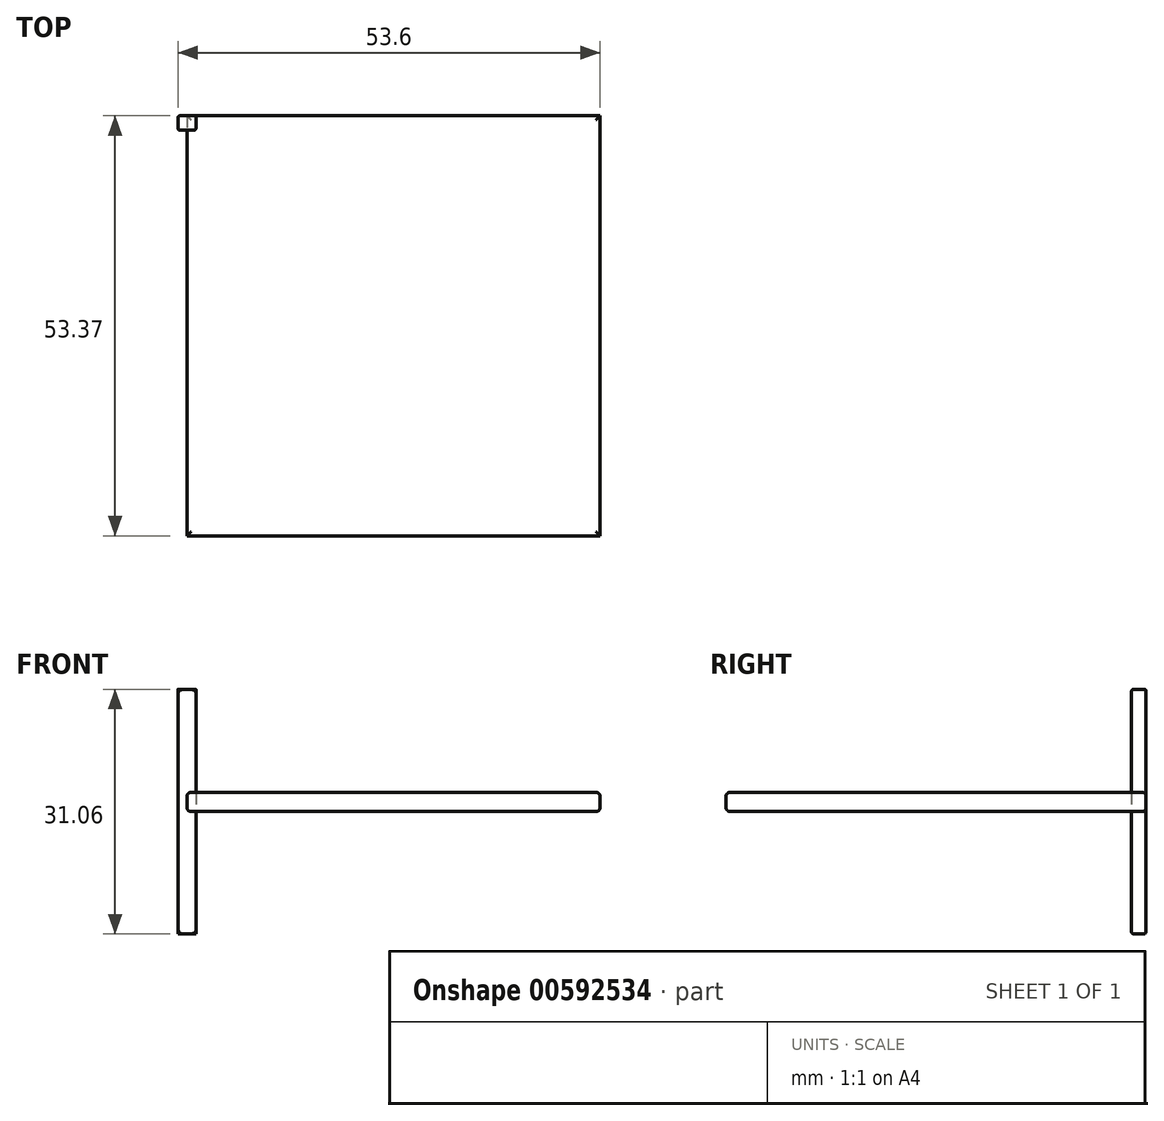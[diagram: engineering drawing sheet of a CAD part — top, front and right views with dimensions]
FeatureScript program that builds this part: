
annotation { "Feature Type Name" : "Feature", "Feature Type Description" : "" }
export const myFeature = defineFeature(function(context is Context, id is Id, definition is map)
    precondition{}
    {
        {
            var Q0;
            Q0=qCreatedBy(makeId("Front.planeOp"),FACE);
            var sketch = newSketch(context, id + "F0", { "sketchPlane" : qUnion([Q0])});
            skLineSegment(sketch, "E0.bottom", {"start": v(-76.14, -76.26) * mm, "end": v(-73.88, -76.26) * mm});
            skLineSegment(sketch, "E0.top", {"start": v(-76.14, -107.32) * mm, "end": v(-73.88, -107.32) * mm});
            skLineSegment(sketch, "E0.left", {"start": v(-76.14, -76.26) * mm, "end": v(-76.14, -107.32) * mm});
            skLineSegment(sketch, "E0.right", {"start": v(-73.88, -76.26) * mm, "end": v(-73.88, -107.32) * mm});
            skLineSegment(sketch, "E1.bottom", {"start": v(-1.13, 15.53) * mm, "end": v(1.13, 15.53) * mm});
            skLineSegment(sketch, "E1.top", {"start": v(-1.13, -15.53) * mm, "end": v(1.13, -15.53) * mm});
            skLineSegment(sketch, "E1.left", {"start": v(-1.13, 15.53) * mm, "end": v(-1.13, -15.53) * mm});
            skLineSegment(sketch, "E1.right", {"start": v(1.13, 15.53) * mm, "end": v(1.13, -15.53) * mm});
            skSolve(sketch);
        }
        {
            var Q0;
            Q0 = qSketchRegion(id + "F0", true);
            extrude(context, id + "F1", {"entities" : qUnion([Q0]), "depth" : 1.86 * mm, "offsetDistance" : 25.4 * mm});
        }
        {
            var Q0;
            Q0=qCreatedBy(makeId("Top.planeOp"),FACE);
            var sketch = newSketch(context, id + "F2", { "sketchPlane" : qUnion([Q0])});
            skLineSegment(sketch, "E2.bottom", {"start": v(0, 0) * mm, "end": v(52.47, 0) * mm});
            skLineSegment(sketch, "E2.top", {"start": v(0, -53.37) * mm, "end": v(52.47, -53.37) * mm});
            skLineSegment(sketch, "E2.left", {"start": v(0, 0) * mm, "end": v(0, -53.37) * mm});
            skLineSegment(sketch, "E2.right", {"start": v(52.47, 0) * mm, "end": v(52.47, -53.37) * mm});
            skSolve(sketch);
        }
        {
            var Q0;
            Q0 = qSketchRegion(id + "F2", true);
            extrude(context, id + "F3", {"entities" : qUnion([Q0]), "depth" : 2.44 * mm, "offsetDistance" : 25.4 * mm});
        }
        {
            var Q0;
            Q0=makeQuery(id+"F1.opExtrude","SWEPT_BODY",BODY,{"disambiguationData":[OSD([sQuery(id+"F0.wireOp",EDGE,"E0.bottom"),sQuery(id+"F0.wireOp",EDGE,"E0.top"),sQuery(id+"F0.wireOp",EDGE,"E0.left"),sQuery(id+"F0.wireOp",EDGE,"E0.right")])]});
            deleteBodies(context, id + "F4", {"entities" : qUnion([Q0])});
        }
        {
            var Q0;
            Q0=makeQuery(id+"F3.opExtrude","CAP_FACE",FACE,{"disambiguationData":[OSD([sQuery(id+"F2.wireOp",EDGE,"E2.bottom"),sQuery(id+"F2.wireOp",EDGE,"E2.top"),sQuery(id+"F2.wireOp",EDGE,"E2.left"),sQuery(id+"F2.wireOp",EDGE,"E2.right")])],"isStart":false});
            var Q1;
            Q1=makeQuery(id+"F3.opExtrude","CAP_FACE",FACE,{"disambiguationData":[OSD([sQuery(id+"F2.wireOp",EDGE,"E2.bottom"),sQuery(id+"F2.wireOp",EDGE,"E2.top"),sQuery(id+"F2.wireOp",EDGE,"E2.left"),sQuery(id+"F2.wireOp",EDGE,"E2.right")])],"isStart":true});
            fillet(context, id + "F5", {"entities" : qUnion([Q0, Q1]), "radius" : 0.5 * mm, "tangentPropagation" : true, "allowEdgeOverflow" : false});
        }
        {
            var Q0;
            Q0=makeQuery(id+"F1.opExtrude","CAP_FACE",FACE,{"disambiguationData":[OSD([sQuery(id+"F0.wireOp",EDGE,"E1.bottom"),sQuery(id+"F0.wireOp",EDGE,"E1.top"),sQuery(id+"F0.wireOp",EDGE,"E1.left"),sQuery(id+"F0.wireOp",EDGE,"E1.right")])],"isStart":false});
            var Q1;
            Q1=makeQuery(id+"F1.opExtrude","CAP_FACE",FACE,{"disambiguationData":[OSD([sQuery(id+"F0.wireOp",EDGE,"E1.bottom"),sQuery(id+"F0.wireOp",EDGE,"E1.top"),sQuery(id+"F0.wireOp",EDGE,"E1.left"),sQuery(id+"F0.wireOp",EDGE,"E1.right")])],"isStart":true});
            fillet(context, id + "F6", {"entities" : qUnion([Q0, Q1]), "radius" : 0.25 * mm, "tangentPropagation" : true, "allowEdgeOverflow" : false});
        }
    });
